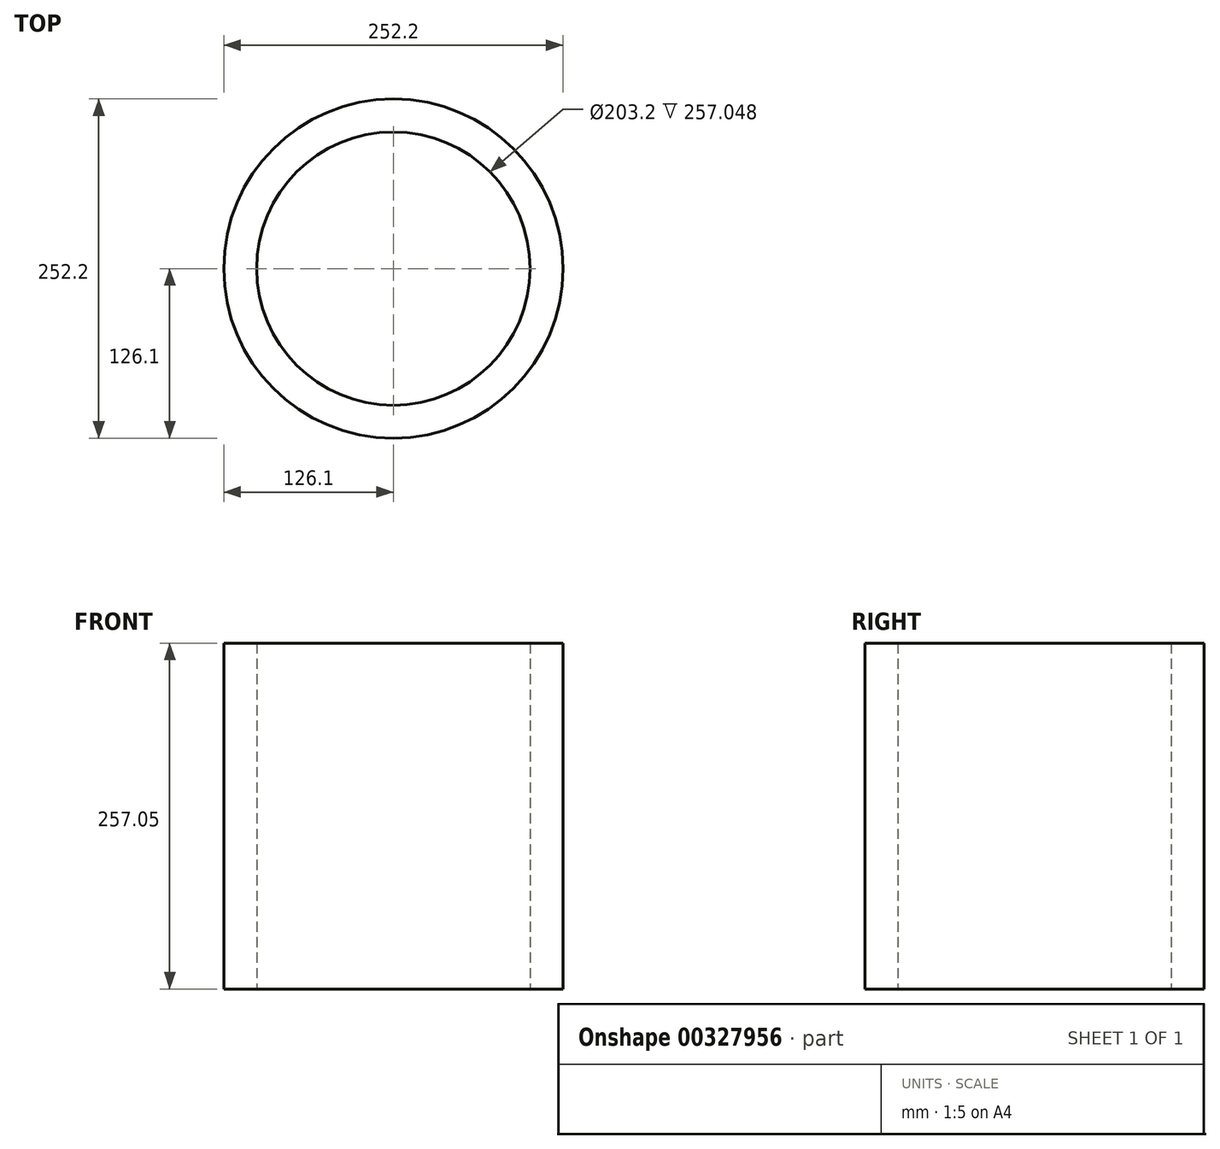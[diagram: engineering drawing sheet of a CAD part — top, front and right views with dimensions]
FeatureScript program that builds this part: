
annotation { "Feature Type Name" : "Feature", "Feature Type Description" : "" }
export const myFeature = defineFeature(function(context is Context, id is Id, definition is map)
    precondition{}
    {
        {
            var Q0;
            Q0=qCreatedBy(makeId("Top.planeOp"),FACE);
            var sketch = newSketch(context, id + "F0", { "sketchPlane" : qUnion([Q0])});
            skCircle(sketch, "E0", {"center": v(0, 0) * mm, "radius": 126.1 * mm});
            skSolve(sketch);
        }
        {
            var Q0;
            Q0 = qSketchRegion(id + "F0", true);
            extrude(context, id + "F1", {"entities" : qUnion([Q0]), "depth" : 106.68 * mm, "offsetDistance" : 25.4 * mm});
        }
        {
            var Q0;
            Q0=sQuery(id+"F0.wireOp",VERTEX,"E0.center");
            var Q1;
            Q1=makeQuery(id+"F1.opExtrude","SWEPT_BODY",BODY,{"disambiguationData":[OSD([sQuery(id+"F0.wireOp",EDGE,"E0")])]});
            hole(context, id + "F2", {"style" : HoleStyle.SIMPLE, "endStyle" : HoleEndStyle.THROUGH, "oppositeDirection" : true, "holeDiameter" : 203.2 * mm, "majorDiameter" : 6.35 * mm, "isTappedThrough" : true, "tappedDepth" : 12.7 * mm, "tapClearance" : 3, "locations" : qUnion([Q0]), "scope" : qUnion([Q1])});
        }
        {
            var Q0;
            Q0=makeQuery(id+"F1.opExtrude","CAP_FACE",FACE,{"disambiguationData":[OSD([sQuery(id+"F0.wireOp",EDGE,"E0")])],"isStart":false});
            extrude(context, id + "F3", {"entities" : qUnion([Q0]), "operationType" : NewBodyOperationType.ADD, "depth" : 150.37 * mm, "offsetDistance" : 25.4 * mm});
        }
    });
